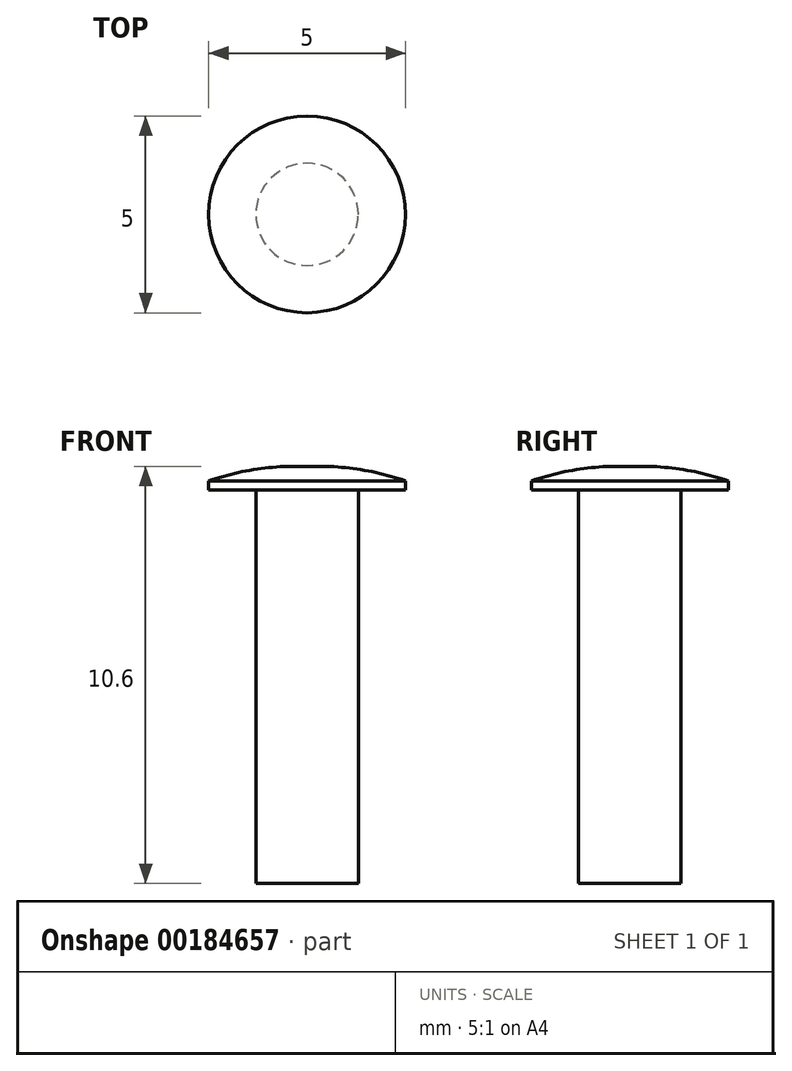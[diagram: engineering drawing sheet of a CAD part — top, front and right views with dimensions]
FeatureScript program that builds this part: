
annotation { "Feature Type Name" : "Feature", "Feature Type Description" : "" }
export const myFeature = defineFeature(function(context is Context, id is Id, definition is map)
    precondition{}
    {
        {
            var Q0;
            Q0=qCreatedBy(makeId("Front.planeOp"),FACE);
            var sketch = newSketch(context, id + "F0", { "sketchPlane" : qUnion([Q0])});
            skLineSegment(sketch, "E0", {"start": v(0, 0) * mm, "end": v(2.5, 0) * mm});
            skLineSegment(sketch, "E1", {"start": v(2.5, 0) * mm, "end": v(2.5, 0.23) * mm});
            skLineSegment(sketch, "E2", {"start": v(0, 0) * mm, "end": v(0, 0.6) * mm});
            skLineSegment(sketch, "E3", {"start": v(0, 0.6) * mm, "end": v(0.3, 0.6) * mm});
            skArc(sketch, "E4", {"start": v(2.5, 0.23) * mm, "mid": v(1.41, 0.5) * mm, "end": v(0.3, 0.6) * mm});
            skSolve(sketch);
        }
        {
            var Q0;
            Q0 = qSketchRegion(id + "F0", true);
            var Q1;
            Q1=sQuery(id+"F0.wireOp",EDGE,"E2");
            revolve(context, id + "F1", {"surfaceOperationType" : NewSurfaceOperationType.NEW, "entities" : qUnion([Q0]), "axis" : qUnion([Q1]), "revolveType" : RevolveType.FULL});
        }
        {
            var Q0;
            Q0=makeQuery(id+"F1.opRevolve","SWEPT_FACE",FACE,{"disambiguationData":[OSD([sQuery(id+"F0.wireOp",EDGE,"E0")])]});
            var sketch = newSketch(context, id + "F2", { "sketchPlane" : qUnion([Q0])});
            skCircle(sketch, "E5", {"center": v(0, 0) * mm, "radius": 1.3 * mm});
            skSolve(sketch);
        }
        {
            var Q0;
            Q0 = qSketchRegion(id + "F2", true);
            extrude(context, id + "F3", {"entities" : qUnion([Q0]), "operationType" : NewBodyOperationType.ADD, "depth" : 10 * mm, "offsetDistance" : 25 * mm});
        }
    });
